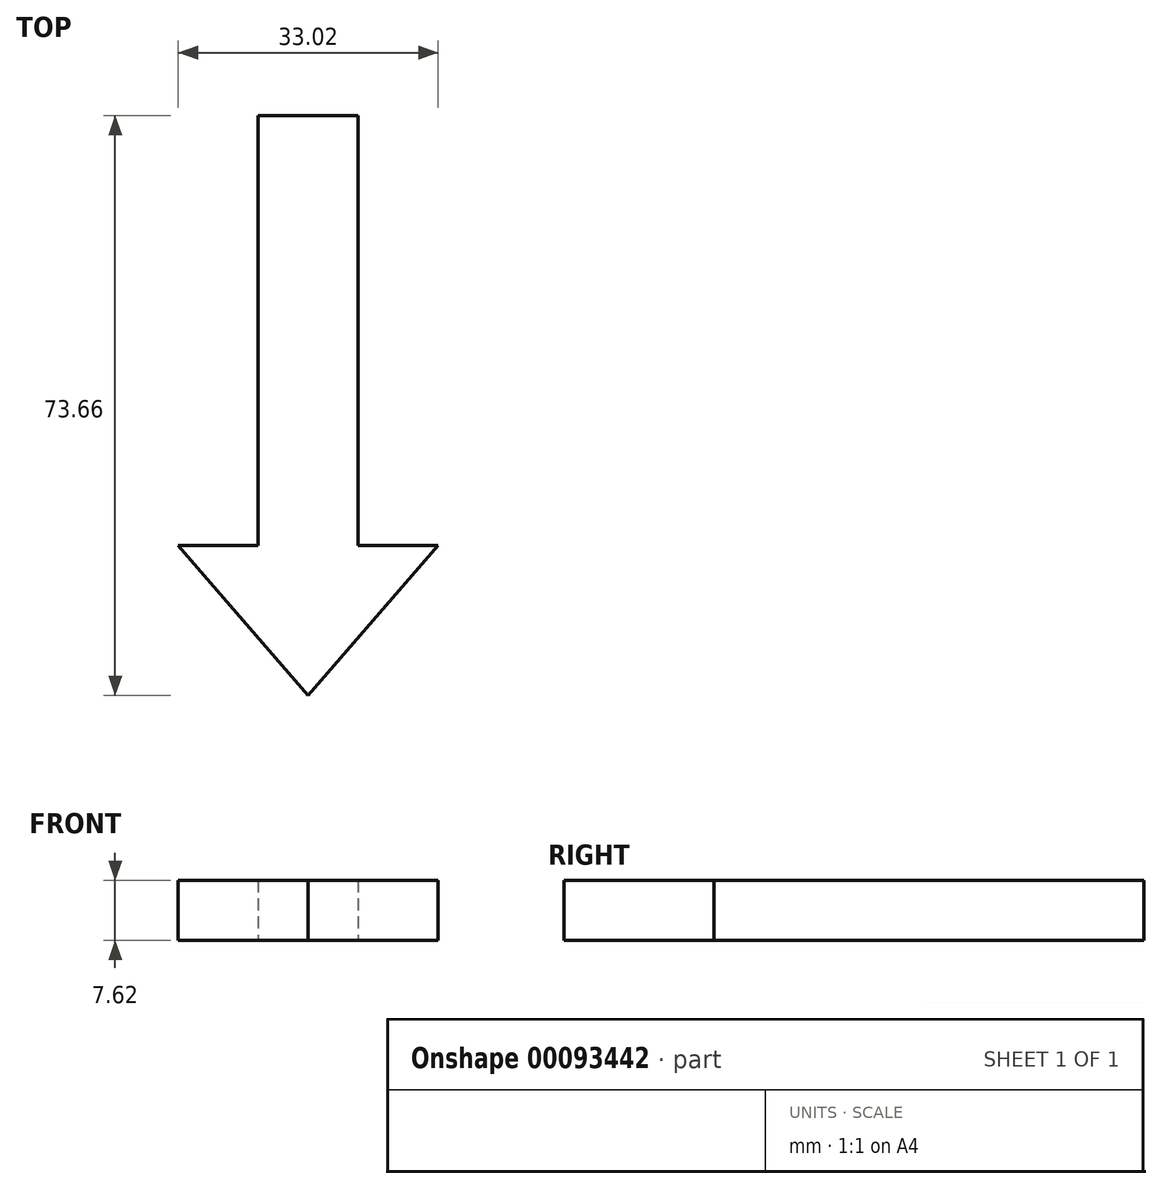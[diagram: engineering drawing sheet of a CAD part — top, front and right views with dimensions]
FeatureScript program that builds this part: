
annotation { "Feature Type Name" : "Feature", "Feature Type Description" : "" }
export const myFeature = defineFeature(function(context is Context, id is Id, definition is map)
    precondition{}
    {
        {
            var Q0;
            Q0=qCreatedBy(makeId("Front.planeOp"),FACE);
            var sketch = newSketch(context, id + "F0", { "sketchPlane" : qUnion([Q0])});
            skLineSegment(sketch, "E0.bottom", {"start": v(0, 0) * mm, "end": v(12.7, 0) * mm});
            skLineSegment(sketch, "E0.top", {"start": v(0, -7.62) * mm, "end": v(12.7, -7.62) * mm});
            skLineSegment(sketch, "E0.left", {"start": v(0, 0) * mm, "end": v(0, -7.62) * mm});
            skLineSegment(sketch, "E0.right", {"start": v(12.7, 0) * mm, "end": v(12.7, -7.62) * mm});
            skSolve(sketch);
        }
        {
            var Q0;
            Q0 = qSketchRegion(id + "F0", true);
            extrude(context, id + "F1", {"entities" : qUnion([Q0]), "depth" : 63.5 * mm});
        }
        {
            var Q0;
            Q0=makeQuery(id+"F1.opExtrude","CAP_FACE",FACE,{"disambiguationData":[OSD([sQuery(id+"F0.wireOp",EDGE,"E0.bottom"),sQuery(id+"F0.wireOp",EDGE,"E0.top"),sQuery(id+"F0.wireOp",EDGE,"E0.left"),sQuery(id+"F0.wireOp",EDGE,"E0.right")])],"isStart":false});
            var sketch = newSketch(context, id + "F2", { "sketchPlane" : qUnion([Q0])});
            skLineSegment(sketch, "E1.bottom", {"start": v(0, 0) * mm, "end": v(12.7, 0) * mm});
            skLineSegment(sketch, "E1.top", {"start": v(0, -7.62) * mm, "end": v(12.7, -7.62) * mm});
            skLineSegment(sketch, "E1.left", {"start": v(0, 0) * mm, "end": v(0, -7.62) * mm});
            skLineSegment(sketch, "E1.right", {"start": v(12.7, 0) * mm, "end": v(12.7, -7.62) * mm});
            skSolve(sketch);
        }
        {
            var Q0;
            Q0=makeQuery(id+"FHTyei9PhtXkGkT_1.boolean.opBoolean","MERGE",FACE,{"derivedFrom":[makeQuery(id+"F1.opExtrude","SWEPT_FACE",FACE,{"disambiguationData":[OSD([sQuery(id+"F0.wireOp",EDGE,"E0.bottom")])]}),makeQuery(id+"FHTyei9PhtXkGkT_1.opExtrude","SWEPT_FACE",FACE,{"disambiguationData":[OSD([sQuery(id+"F2.wireOp",EDGE,"E1.bottom")])]})]});
            var sketch = newSketch(context, id + "F3", { "sketchPlane" : qUnion([Q0])});
            skLineSegment(sketch, "E2", {"start": v(-10.16, -54.61) * mm, "end": v(22.86, -54.6) * mm});
            skLineSegment(sketch, "E3", {"start": v(22.86, -54.6) * mm, "end": v(6.35, -73.66) * mm});
            skLineSegment(sketch, "E4", {"start": v(6.35, -73.66) * mm, "end": v(-10.16, -54.6) * mm});
            skLineSegment(sketch, "E5", {"start": v(6.35, -73.66) * mm, "end": v(6.35, -63.5) * mm});
            skSolve(sketch);
        }
        {
            var Q0;
            Q0 = qSketchRegion(id + "F3", true);
            extrude(context, id + "F4", {"entities" : qUnion([Q0]), "operationType" : NewBodyOperationType.ADD, "oppositeDirection" : true, "depth" : 7.62 * mm});
        }
    });
